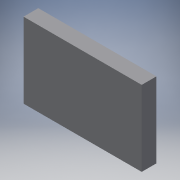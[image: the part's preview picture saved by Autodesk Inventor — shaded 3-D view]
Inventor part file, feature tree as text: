
AUTODESK INVENTOR PART (.ipt)
format: ipt  version: 2016 (Build 200138000, 138)  size: 82,944 bytes
history: native  units: in
note: dims shown in document units (in); Inventor stores cm internally (conversion verified against a paired STEP export)
features: extrude x1, sketch x1
ambient origin geometry x8: Origin, YZ Plane, XZ Plane, XY Plane, X Axis, Y Axis, Z Axis, Center Point
bodies: Solid1 (feature_tree)
feature tree (2):
  extrude  "Extrusion1"  Depth=2.55in
  sketch  "Sketch1"  dims[d0=4.0in d1=2.55in d2=0.5in d3=0.0in]
